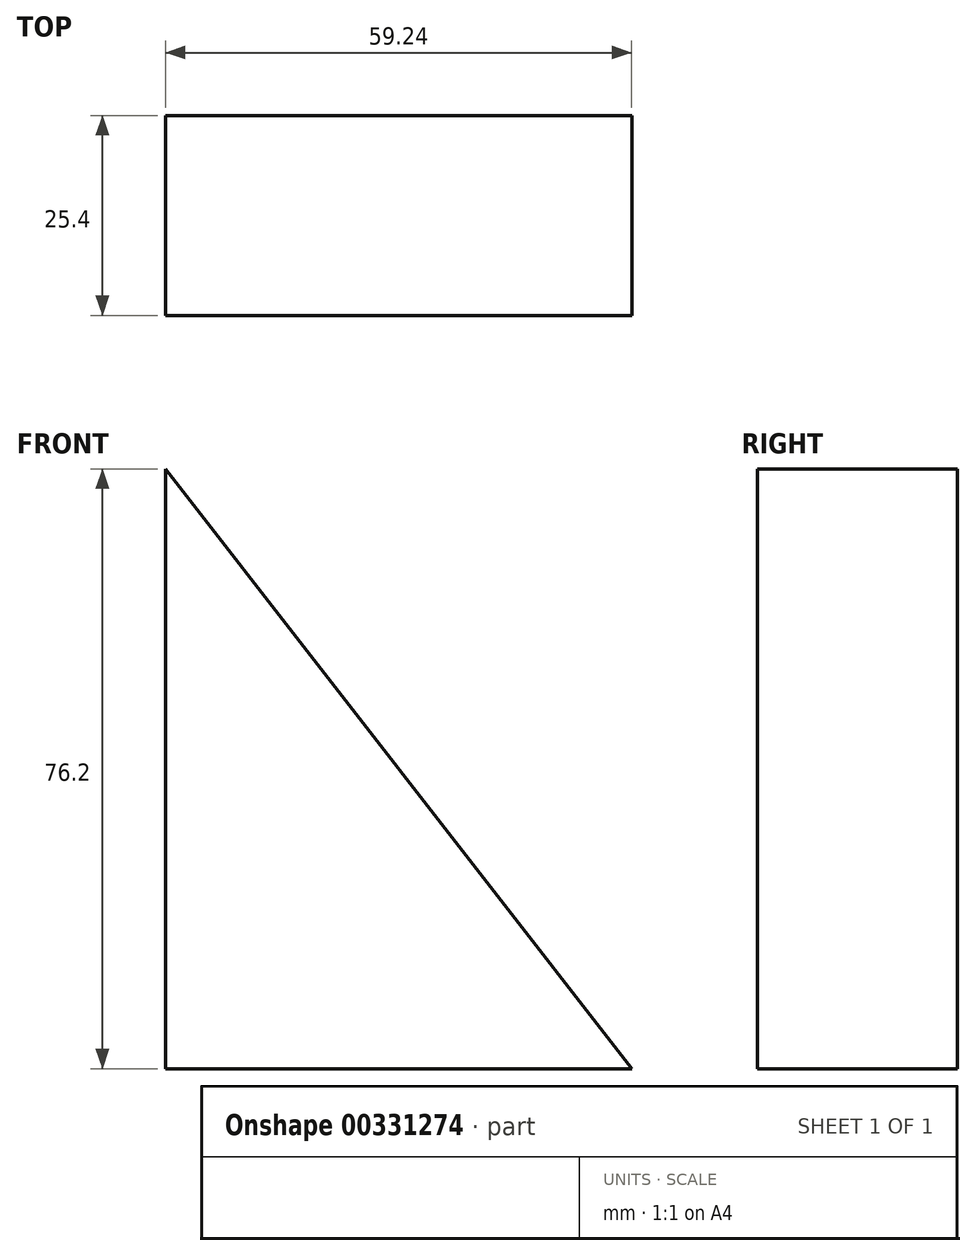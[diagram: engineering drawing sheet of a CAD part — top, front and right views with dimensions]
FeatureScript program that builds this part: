
annotation { "Feature Type Name" : "Feature", "Feature Type Description" : "" }
export const myFeature = defineFeature(function(context is Context, id is Id, definition is map)
    precondition{}
    {
        {
            var Q0;
            Q0=qCreatedBy(makeId("Front.planeOp"),FACE);
            var sketch = newSketch(context, id + "F0", { "sketchPlane" : qUnion([Q0])});
            skLineSegment(sketch, "E0", {"start": v(0, 0) * mm, "end": v(0, 76.2) * mm});
            skLineSegment(sketch, "E1", {"start": v(0, 76.2) * mm, "end": v(59.24, 0) * mm});
            skLineSegment(sketch, "E2", {"start": v(59.24, 0) * mm, "end": v(0, 0) * mm});
            skSolve(sketch);
        }
        {
            var Q0;
            Q0 = qSketchRegion(id + "F0", true);
            extrude(context, id + "F1", {"entities" : qUnion([Q0]), "depth" : 25.4 * mm});
        }
    });
